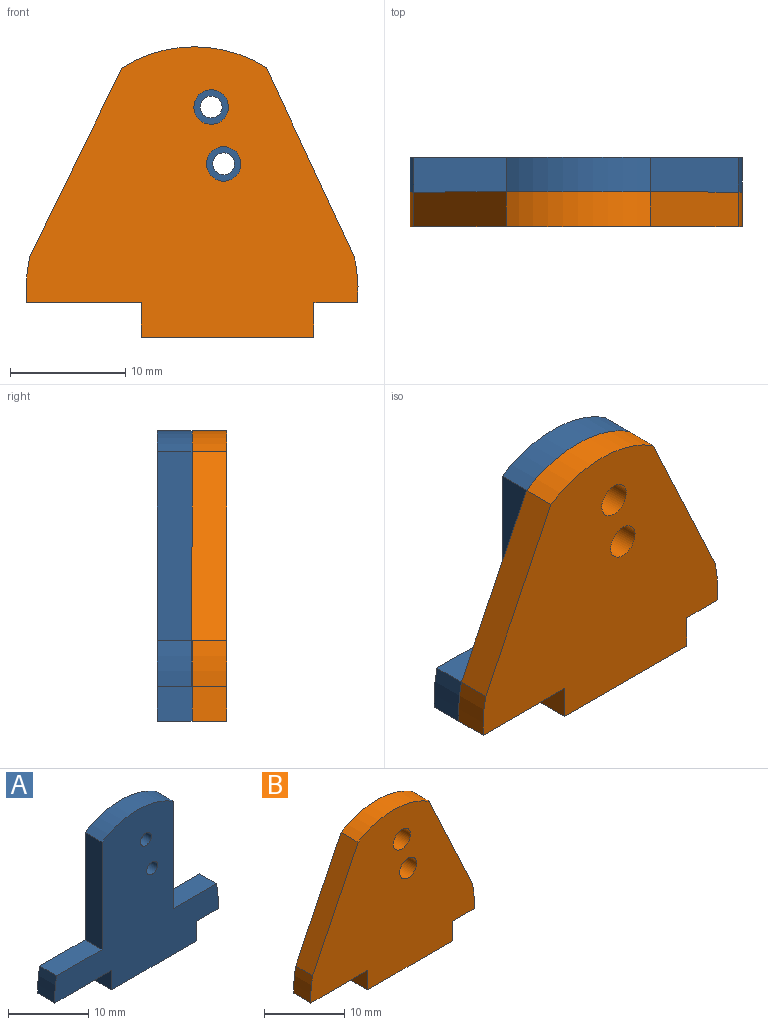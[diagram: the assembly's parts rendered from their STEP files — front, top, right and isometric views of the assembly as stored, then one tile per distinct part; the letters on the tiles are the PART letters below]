
ASSEMBLY  parts=2 mates=1
PART A: 17 faces, bbox 28.9x3x25.2 mm
  f0: cylinder r=14.43mm len=4mm, axis (0,1,0), area 12.1mm2, adj f1,f14,f15,f16
  f1: plane 10x3mm, normal (0,0,-1), area 30mm2, adj f0,f2,f15,f16
  f2: plane 3x3mm, normal (-1,0,0), area 9mm2, adj f1,f3,f15,f16
  f3: plane 15x3mm, normal (0,0,-1), area 45mm2, adj f2,f4,f15,f16
  f4: plane 3x3mm, normal (1,0,0), area 9mm2, adj f3,f5,f15,f16
  f5: plane 3.81x3mm, normal (0,0,-1), area 11.4mm2, adj f4,f6,f15,f16
  f6: extruded ~3x1.39mm, area 4.2mm2, adj f5,f7,f15,f16
  f7: cylinder r=14.43mm len=3mm, axis (0,1,0), area 7.9mm2, adj f6,f8,f15,f16
  f8: plane 7.64x3mm, normal (0,0,1), area 22.9mm2, adj f7,f9,f15,f16
  f9: plane 16.41x3mm, normal (1,0,0), area 49.2mm2, adj f8,f10,f15,f16
  f10: cylinder r=11.7mm len=12.53mm, axis (0,1,0), area 39.7mm2, adj f9,f11,f15,f16
  f11: plane 16.41x3mm, normal (-1,0,0), area 49.2mm2, adj f10,f14,f15,f16
  f12: cylinder r=0.95mm len=3mm, axis (0,1,0), area 17.9mm2, adj f15,f16
  f13: cylinder r=0.95mm len=3mm, axis (0,1,0), area 17.9mm2, adj f15,f16
  f14: plane 8.02x3mm, normal (0,0,1), area 24.1mm2, adj f0,f11,f15,f16
  f15: plane 28.85x25.23mm, normal (0,-1,0), area 375.3mm2, adj f0,f1,f2,f3,f4,f5,f6,f7
  f16: plane 28.85x25.23mm, normal (0,1,0), area 375.3mm2, adj f0,f1,f2,f3,f4,f5,f6,f7
PART B: 15 faces, bbox 28.9x3x25.2 mm
  f0: cylinder r=14.43mm len=4mm, axis (0,1,0), area 12.1mm2, adj f1,f12,f13,f14
  f1: plane 10x3mm, normal (0,0,-1), area 30mm2, adj f0,f2,f13,f14
  f2: plane 3x3mm, normal (-1,0,0), area 9mm2, adj f1,f3,f13,f14
  f3: plane 15x3mm, normal (0,0,-1), area 45mm2, adj f2,f4,f13,f14
  f4: plane 3x3mm, normal (1,0,0), area 9mm2, adj f3,f5,f13,f14
  f5: plane 3.81x3mm, normal (0,0,-1), area 11.4mm2, adj f4,f6,f13,f14
  f6: extruded ~3x1.39mm, area 4.2mm2, adj f5,f7,f13,f14
  f7: cylinder r=14.43mm len=3mm, axis (0,1,0), area 7.9mm2, adj f6,f8,f13,f14
  f8: plane 16.41x7.64mm, normal (0.91,0,0.42), area 54.3mm2, adj f7,f9,f13,f14
  f9: cylinder r=11.7mm len=12.53mm, axis (0,1,0), area 39.7mm2, adj f8,f12,f13,f14
  f10: cylinder r=1.5mm len=3mm, axis (0,1,0), area 28.3mm2, adj f13,f14
  f11: cylinder r=1.5mm len=3mm, axis (0,1,0), area 28.3mm2, adj f13,f14
  f12: plane 16.41x8.02mm, normal (-0.9,0,0.44), area 54.8mm2, adj f0,f9,f13,f14
  f13: plane 28.85x25.23mm, normal (0,-1,0), area 495.3mm2, adj f0,f1,f2,f3,f4,f5,f6,f7
  f14: plane 28.85x25.23mm, normal (0,1,0), area 495.3mm2, adj f0,f1,f2,f3,f4,f5,f6,f7
PLACE A t=(-4.16,0.82,3.66)mm
PLACE B t=(-4.16,-2.18,3.66)mm
MATE fastened B.f14 <-> A.f15  axis (0,1,0) through (3.34,-2.18,-7.34)mm
